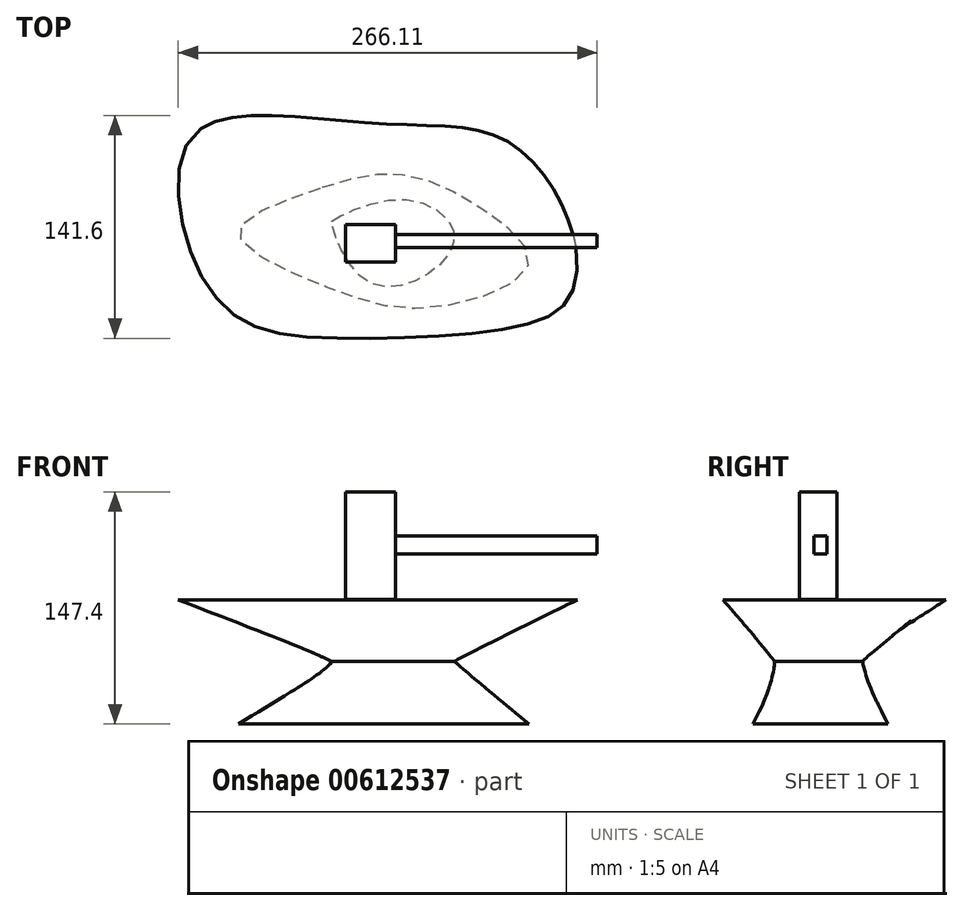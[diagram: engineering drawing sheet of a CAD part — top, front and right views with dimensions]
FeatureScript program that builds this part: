
annotation { "Feature Type Name" : "Feature", "Feature Type Description" : "" }
export const myFeature = defineFeature(function(context is Context, id is Id, definition is map)
    precondition{}
    {
        {
            var Q0;
            Q0=qCreatedBy(makeId("Top.planeOp"),FACE);
            var sketch = newSketch(context, id + "F0", { "sketchPlane" : qUnion([Q0])});
            skFitSpline(sketch, "E0", {"points": [v(-43.2, 20.33) * mm, v(13.16, 32.3) * mm, v(65.52, 11.83) * mm, v(97.41, -25.38) * mm, v(37.08, -52.76) * mm, v(-30.7, -39.74) * mm, v(-86.78, -5.45) * mm, v(-43.2, 20.33) * mm]});
            skSolve(sketch);
        }
        {
            var Q0;
            Q0=qCreatedBy(makeId("Top.planeOp"),FACE);
            cPlane(context, id + "F1", {"entities" : qUnion([Q0]), "cplaneType" : CPlaneType.OFFSET, "offset" : 78.8 * mm, "width" : 150 * mm, "height" : 150 * mm});
        }
        {
            var Q0;
            Q0=qCreatedBy(id+"F1.planeOp",FACE);
            var sketch = newSketch(context, id + "F2", { "sketchPlane" : qUnion([Q0])});
            skFitSpline(sketch, "E1", {"points": [v(-110.44, 61) * mm, v(0, 64.2) * mm, v(83.06, 53.3) * mm, v(124.53, -2.26) * mm, v(122.93, -47.44) * mm, v(83.6, -66.05) * mm, v(-23.79, -72.16) * mm, v(-90.5, -56.75) * mm, v(-122.93, 4.12) * mm, v(-110.44, 61) * mm]});
            skSolve(sketch);
        }
        {
            var Q0;
            Q0=qCreatedBy(makeId("Top.planeOp"),FACE);
            cPlane(context, id + "F3", {"entities" : qUnion([Q0]), "cplaneType" : CPlaneType.OFFSET, "offset" : 39.9 * mm, "width" : 150 * mm, "height" : 150 * mm});
        }
        {
            var Q0;
            Q0=qCreatedBy(id+"F3.planeOp",FACE);
            var sketch = newSketch(context, id + "F4", { "sketchPlane" : qUnion([Q0])});
            skFitSpline(sketch, "E2", {"points": [v(-26.45, 2.8) * mm, v(17.94, 16.08) * mm, v(50.1, -5.71) * mm, v(31.23, -32.83) * mm, v(-7.84, -34.16) * mm, v(-27.51, 0) * mm, v(-26.45, 2.8) * mm]});
            skSolve(sketch);
        }
        {
            var Q0;
            Q0=makeQuery(id+"F4.imprint","IMPRINT",FACE,{"disambiguationData":[TD([[makeQuery(id+"F4.imprint","IMPRINT",EDGE,{"derivedFrom":sQuery(id+"F4.wireOp",EDGE,"E2")}),-1.0]])]});
            var Q1;
            Q1=makeQuery(id+"F0.imprint","IMPRINT",FACE,{"disambiguationData":[TD([[makeQuery(id+"F0.imprint","IMPRINT",EDGE,{"derivedFrom":sQuery(id+"F0.wireOp",EDGE,"E0")}),-1.0]])]});
            loft(context, id + "F5", {"sheetProfilesArray" : [{ "sheetProfileEntities" : qUnion([Q0]) }, { "sheetProfileEntities" : qUnion([Q1]) }]});
        }
        {
            var Q1;
            Q1=makeQuery(id+"F2.imprint","IMPRINT",FACE,{"disambiguationData":[TD([[makeQuery(id+"F2.imprint","IMPRINT",EDGE,{"derivedFrom":sQuery(id+"F2.wireOp",EDGE,"E1")}),-1.0]])]});
            var Q2;
            Q2=makeQuery(id+"F5.opLoft","CAP_FACE",FACE,{"disambiguationData":[OSD([makeQuery(id+"F4.imprint","IMPRINT",FACE,{"disambiguationData":[TD([[makeQuery(id+"F4.imprint","IMPRINT",EDGE,{"derivedFrom":sQuery(id+"F4.wireOp",EDGE,"E2")}),-1.0]])]})])],"isStart":true});
            loft(context, id + "F6", {"operationType" : NewBodyOperationType.ADD, "sheetProfilesArray" : [{ "sheetProfileEntities" : qUnion([Q1]) }, { "sheetProfileEntities" : qUnion([Q2]) }]});
        }
        {
            var Q0;
            Q0=qCreatedBy(makeId("Top.planeOp"),FACE);
            cPlane(context, id + "F7", {"entities" : qUnion([Q0]), "cplaneType" : CPlaneType.OFFSET, "offset" : 79 * mm, "width" : 150 * mm, "height" : 150 * mm});
        }
        {
            var Q0;
            Q0=qCreatedBy(id+"F7.planeOp",FACE);
            var sketch = newSketch(context, id + "F8", { "sketchPlane" : qUnion([Q0])});
            skLineSegment(sketch, "E3.bottom", {"start": v(-18.83, 0) * mm, "end": v(12.92, 0) * mm});
            skLineSegment(sketch, "E3.top", {"start": v(-18.83, -23.8) * mm, "end": v(12.92, -23.8) * mm});
            skLineSegment(sketch, "E3.left", {"start": v(-18.83, 0) * mm, "end": v(-18.83, -23.8) * mm});
            skLineSegment(sketch, "E3.right", {"start": v(12.92, 0) * mm, "end": v(12.92, -23.8) * mm});
            skSolve(sketch);
        }
        {
            var Q0;
            Q0=makeQuery(id+"F8.imprint","IMPRINT",FACE,{"disambiguationData":[TD([[makeQuery(id+"F8.imprint","IMPRINT",EDGE,{"derivedFrom":sQuery(id+"F8.wireOp",EDGE,"E3.bottom")}),-1.0]])]});
            extrude(context, id + "F9", {"entities" : qUnion([Q0]), "operationType" : NewBodyOperationType.ADD, "depth" : 68.4 * mm, "offsetDistance" : 25 * mm});
        }
        {
            var Q0;
            Q0=makeQuery(id+"F9.opExtrude","SWEPT_FACE",FACE,{"disambiguationData":[OSD([sQuery(id+"F8.wireOp",EDGE,"E3.right")])]});
            var sketch = newSketch(context, id + "F10", { "sketchPlane" : qUnion([Q0])});
            skLineSegment(sketch, "E4.bottom", {"start": v(-14.6, 119.3) * mm, "end": v(-6.4, 119.3) * mm});
            skLineSegment(sketch, "E4.top", {"start": v(-14.6, 108.15) * mm, "end": v(-6.4, 108.15) * mm});
            skLineSegment(sketch, "E4.left", {"start": v(-14.6, 119.3) * mm, "end": v(-14.6, 108.15) * mm});
            skLineSegment(sketch, "E4.right", {"start": v(-6.4, 119.3) * mm, "end": v(-6.4, 108.15) * mm});
            skSolve(sketch);
        }
        {
            var Q0;
            Q0=makeQuery(id+"F10.imprint","IMPRINT",FACE,{"disambiguationData":[TD([[makeQuery(id+"F10.imprint","IMPRINT",EDGE,{"derivedFrom":sQuery(id+"F10.wireOp",EDGE,"E4.bottom")}),-1.0]])]});
            extrude(context, id + "F11", {"entities" : qUnion([Q0]), "operationType" : NewBodyOperationType.ADD, "depth" : 128.1 * mm, "offsetDistance" : 25 * mm});
        }
    });
